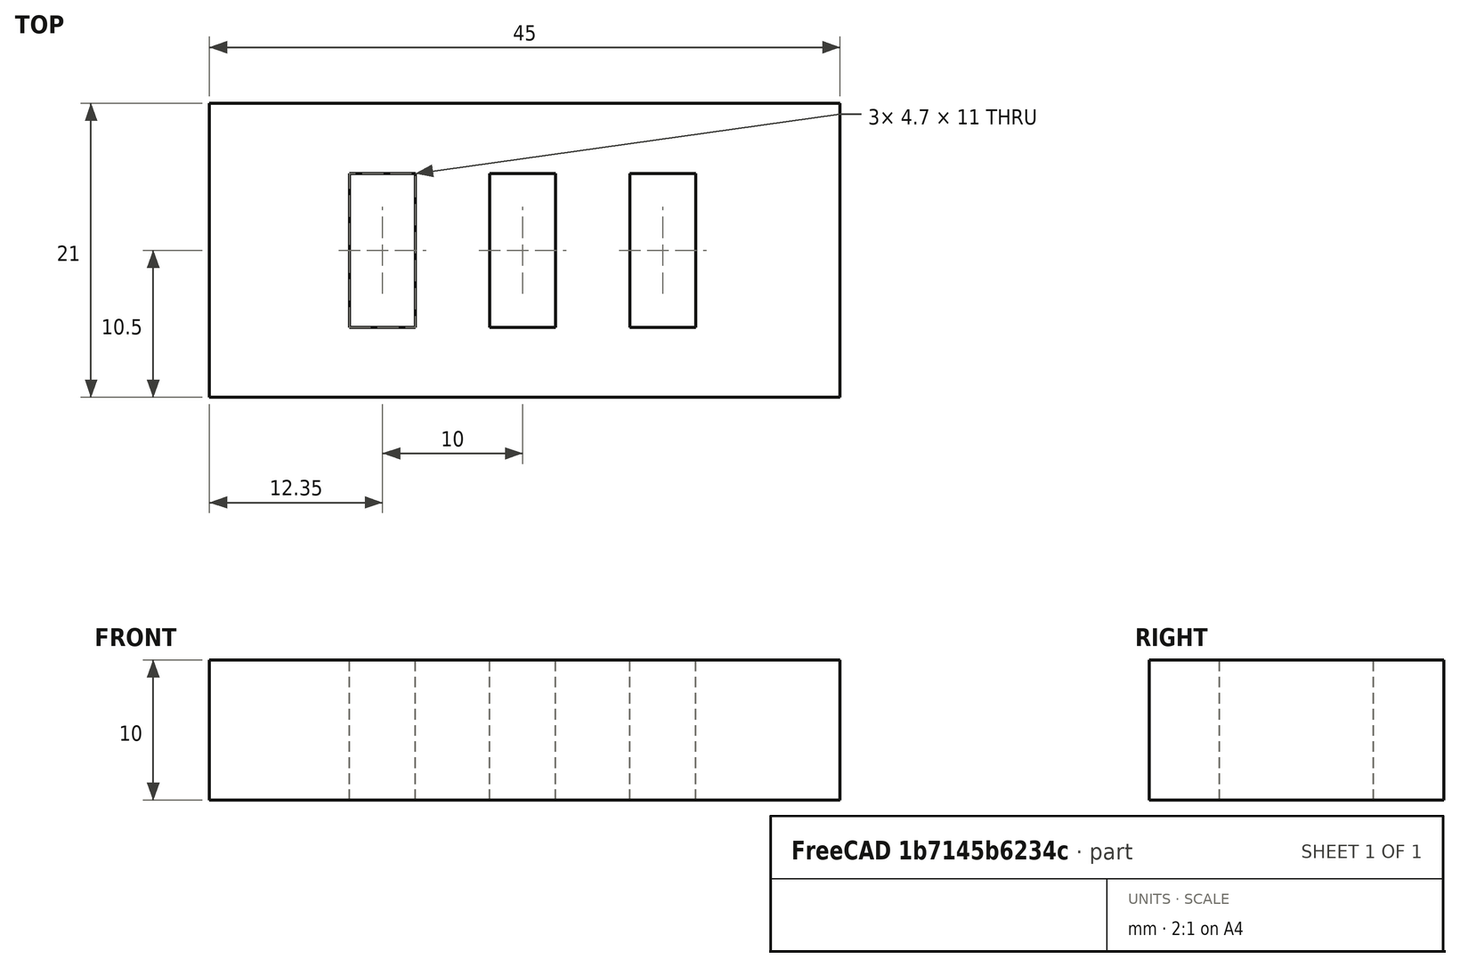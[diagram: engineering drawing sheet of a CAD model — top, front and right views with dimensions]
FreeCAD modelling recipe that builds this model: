
FCSTD DOCUMENT  (FreeCAD 0.20R29177 (Git))
Label: Video8
License: All rights reserved
LicenseURL: http://en.wikipedia.org/wiki/All_rights_reserved
objects: Part::Box×4, Part::Fuse×2, Part::Cut×1
note: 7 computed .brp shape members not serialized (recipe doc carries the construction recipe); baked Part::Feature solids carry a one-line shape summary decoded from their .brp

FEATURE [Part::Box] Box  label="Cubo_base"
  AttacherType = Attacher::AttachEngine3D
  Height = 10
  Length = 45
  Width = 21
FEATURE [Part::Box] Box001  label="Cubo_resta1"
  AttacherType = Attacher::AttachEngine3D
  Height = 13
  Length = 4.7
  Placement = pos=(10,5,0) rot=(0,0,1;0rad)
  Width = 11
FEATURE [Part::Box] Box002  label="Cubo_resta002"
  AttacherType = Attacher::AttachEngine3D
  Height = 13
  Length = 4.7
  Placement = pos=(20,5,0) rot=(0,0,1;0rad)
  Width = 11
FEATURE [Part::Box] Box003  label="Cubo_resta003"
  AttacherType = Attacher::AttachEngine3D
  Height = 13
  Length = 4.7
  Placement = pos=(30,5,0) rot=(0,0,1;0rad)
  Width = 11
FEATURE [Part::Fuse] Fusion
  Base = -> Box001
  Tool = -> Box002
FEATURE [Part::Fuse] Fusion001  label="ranuras"
  Base = -> Box003
  Tool = -> Fusion
FEATURE [Part::Cut] Cut
  Base = -> Box
  Tool = -> Fusion001
